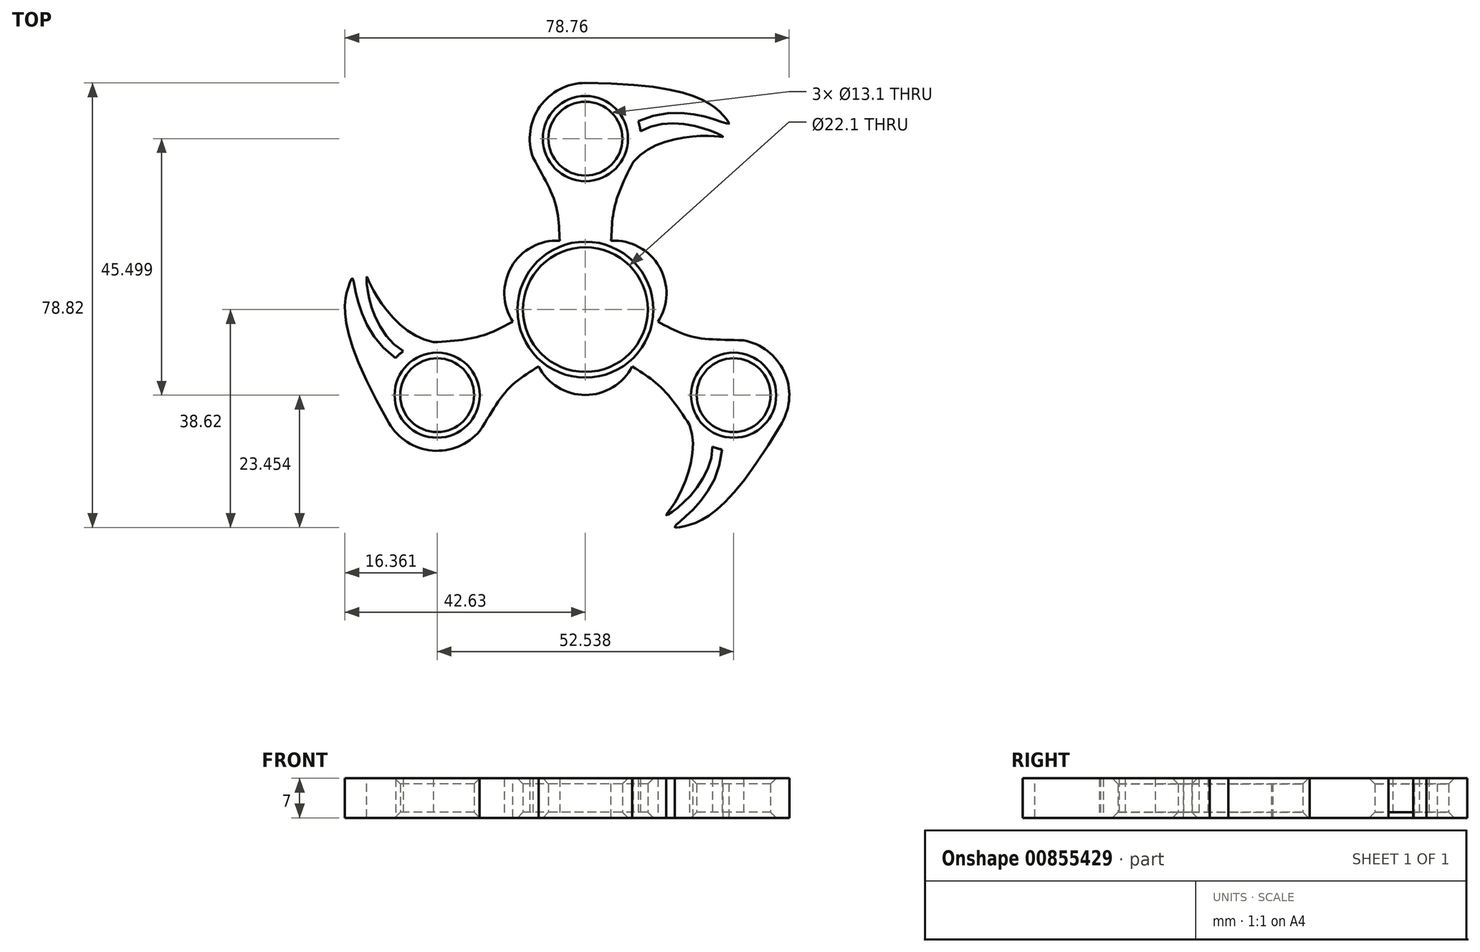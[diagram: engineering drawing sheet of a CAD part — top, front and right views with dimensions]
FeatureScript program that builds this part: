
annotation { "Feature Type Name" : "Feature", "Feature Type Description" : "" }
export const myFeature = defineFeature(function(context is Context, id is Id, definition is map)
    precondition{}
    {
        {
            var Q0;
            Q0=qCreatedBy(makeId("Top.planeOp"),FACE);
            var sketch = newSketch(context, id + "F0", { "sketchPlane" : qUnion([Q0])});
            skCircle(sketch, "E0", {"center": v(0, 0) * mm, "radius": 11.05 * mm});
            skCircle(sketch, "E1", {"center": v(0, 30.33) * mm, "radius": 6.55 * mm});
            skFitSpline(sketch, "E2.MirrorCS", {"points": [v(-9.29, 27) * mm, v(-5.37, 18.96) * mm, v(-4.56, 12.23) * mm], "startDerivative": vector(9.19, -18.15) * mm, "endDerivative": vector(0.68, -14.58) * mm});
            skFitSpline(sketch, "E3", {"points": [v(9.78, 31.66) * mm, v(24.36, 30.7) * mm, v(22.84, 30.77) * mm, v(8.48, 26.22) * mm], "startDerivative": vector(41.62, 23.35) * mm, "endDerivative": vector(-24.9, -29.83) * mm});
            skLineSegment(sketch, "E4", {"start": v(4.56, 12.23) * mm, "end": v(4.56, 12.23) * mm});
            skFitSpline(sketch, "E5", {"points": [v(9.72, 28.65) * mm, v(5.37, 18.96) * mm, v(4.56, 12.23) * mm], "startDerivative": vector(-9.19, -18.15) * mm, "endDerivative": vector(-0.68, -14.58) * mm});
            skArc(sketch, "E6", {"start": v(9.78, 31.66) * mm, "mid": v(9.61, 32.54) * mm, "end": v(9.38, 33.4) * mm});
            skLineSegment(sketch, "E7", {"start": v(9.38, 33.4) * mm, "end": v(9.38, 33.4) * mm});
            skFitSpline(sketch, "E8", {"points": [v(0, 40.2) * mm, v(24.6, 34.26) * mm, v(25.43, 32.97) * mm, v(9.38, 33.4) * mm], "startDerivative": vector(114.25, -0.66) * mm, "endDerivative": vector(-61.81, -28.86) * mm});
            skArc(sketch, "E9", {"start": v(0, 40.2) * mm, "mid": v(-8.07, 36) * mm, "end": v(-9.29, 27) * mm});
            skCircle(sketch, "E10", {"center": v(26.27, -15.17) * mm, "radius": 6.55 * mm});
            skFitSpline(sketch, "E11.MirrorCS", {"points": [v(28.03, -5.46) * mm, v(19.1, -4.84) * mm, v(12.87, -2.16) * mm], "startDerivative": vector(-20.31, 1.12) * mm, "endDerivative": vector(-12.97, 6.7) * mm});
            skFitSpline(sketch, "E12", {"points": [v(22.53, -24.3) * mm, v(14.4, -36.45) * mm, v(15.23, -35.17) * mm, v(18.46, -20.45) * mm], "startDerivative": vector(-0.6, -47.72) * mm, "endDerivative": vector(-13.38, 36.47) * mm});
            skLineSegment(sketch, "E13", {"start": v(8.3, -10.07) * mm, "end": v(8.3, -10.07) * mm});
            skFitSpline(sketch, "E14", {"points": [v(19.95, -22.74) * mm, v(13.74, -14.13) * mm, v(8.3, -10.07) * mm], "startDerivative": vector(-11.12, 17.03) * mm, "endDerivative": vector(-12.29, 7.88) * mm});
            skArc(sketch, "E15", {"start": v(22.53, -24.3) * mm, "mid": v(23.37, -24.6) * mm, "end": v(24.24, -24.82) * mm});
            skFitSpline(sketch, "E16", {"points": [v(34.81, -20.1) * mm, v(17.37, -38.43) * mm, v(15.84, -38.51) * mm, v(24.24, -24.82) * mm], "startDerivative": vector(-57.7, -98.62) * mm, "endDerivative": vector(5.91, 67.96) * mm});
            skArc(sketch, "E17", {"start": v(34.81, -20.1) * mm, "mid": v(35.22, -11.02) * mm, "end": v(28.03, -5.46) * mm});
            skCircle(sketch, "E18", {"center": v(-26.27, -15.17) * mm, "radius": 6.55 * mm});
            skFitSpline(sketch, "E19.MirrorCS", {"points": [v(-18.74, -21.54) * mm, v(-13.74, -14.13) * mm, v(-8.3, -10.07) * mm], "startDerivative": vector(11.12, 17.03) * mm, "endDerivative": vector(12.29, 7.88) * mm});
            skFitSpline(sketch, "E20", {"points": [v(-32.3, -7.37) * mm, v(-38.77, 5.75) * mm, v(-38.07, 4.4) * mm, v(-26.94, -5.76) * mm], "startDerivative": vector(-41.03, 24.37) * mm, "endDerivative": vector(38.28, -6.64) * mm});
            skLineSegment(sketch, "E21", {"start": v(-12.87, -2.16) * mm, "end": v(-12.87, -2.16) * mm});
            skFitSpline(sketch, "E22", {"points": [v(-29.67, -5.9) * mm, v(-19.1, -4.84) * mm, v(-12.87, -2.16) * mm], "startDerivative": vector(20.31, 1.12) * mm, "endDerivative": vector(12.97, 6.7) * mm});
            skArc(sketch, "E23", {"start": v(-32.3, -7.37) * mm, "mid": v(-32.99, -7.94) * mm, "end": v(-33.61, -8.58) * mm});
            skFitSpline(sketch, "E24", {"points": [v(-34.81, -20.1) * mm, v(-41.96, 4.17) * mm, v(-41.27, 5.54) * mm, v(-33.61, -8.58) * mm], "startDerivative": vector(-56.55, 99.28) * mm, "endDerivative": vector(55.9, -39.1) * mm});
            skArc(sketch, "E25", {"start": v(-34.81, -20.1) * mm, "mid": v(-27.15, -25) * mm, "end": v(-18.74, -21.54) * mm});
            skArc(sketch, "E26", {"start": v(12.87, -2.16) * mm, "mid": v(13.11, 7.57) * mm, "end": v(4.56, 12.23) * mm});
            skArc(sketch, "E27.1.0", {"start": v(-4.56, 12.23) * mm, "mid": v(-13.11, 7.57) * mm, "end": v(-12.87, -2.16) * mm});
            skArc(sketch, "E27.2.0", {"start": v(-8.3, -10.07) * mm, "mid": v(0, -15.14) * mm, "end": v(8.3, -10.07) * mm});
            skSolve(sketch);
        }
        {
            var Q0;
            Q0=makeQuery(id+"F0.imprint","IMPRINT",FACE,{"disambiguationData":[TD([[makeQuery(id+"F0.imprint","IMPRINT",EDGE,{"derivedFrom":sQuery(id+"F0.wireOp",EDGE,"E0")}),-1.0]])]});
            extrude(context, id + "F1", {"entities" : qUnion([Q0]), "depth" : 7 * mm, "offsetDistance" : 25 * mm});
        }
        {
            var Q0;
            Q0=makeQuery(id+"F1.opExtrude","CAP_EDGE",EDGE,{"disambiguationData":[OSD([sQuery(id+"F0.wireOp",EDGE,"E0")])],"isStart":true});
            var Q1;
            Q1=makeQuery(id+"F1.opExtrude","CAP_EDGE",EDGE,{"disambiguationData":[OSD([sQuery(id+"F0.wireOp",EDGE,"E10")])],"isStart":true});
            var Q2;
            Q2=makeQuery(id+"F1.opExtrude","CAP_EDGE",EDGE,{"disambiguationData":[OSD([sQuery(id+"F0.wireOp",EDGE,"E1")])],"isStart":true});
            var Q3;
            Q3=makeQuery(id+"F1.opExtrude","CAP_EDGE",EDGE,{"disambiguationData":[OSD([sQuery(id+"F0.wireOp",EDGE,"E18")])],"isStart":true});
            var Q4;
            Q4=makeQuery(id+"F1.opExtrude","CAP_EDGE",EDGE,{"disambiguationData":[OSD([sQuery(id+"F0.wireOp",EDGE,"E1")])],"isStart":false});
            var Q5;
            Q5=makeQuery(id+"F1.opExtrude","CAP_EDGE",EDGE,{"disambiguationData":[OSD([sQuery(id+"F0.wireOp",EDGE,"E18")])],"isStart":false});
            var Q6;
            Q6=makeQuery(id+"F1.opExtrude","SWEPT_FACE",FACE,{"disambiguationData":[OSD([sQuery(id+"F0.wireOp",EDGE,"E0")])]});
            var Q7;
            Q7=makeQuery(id+"F1.opExtrude","CAP_EDGE",EDGE,{"disambiguationData":[OSD([sQuery(id+"F0.wireOp",EDGE,"E10")])],"isStart":false});
            chamfer(context, id + "F2", {"entities" : qUnion([Q0, Q1, Q2, Q3, Q4, Q5, Q6, Q7]), "width" : 1 * mm, "tangentPropagation" : true});
        }
    });
